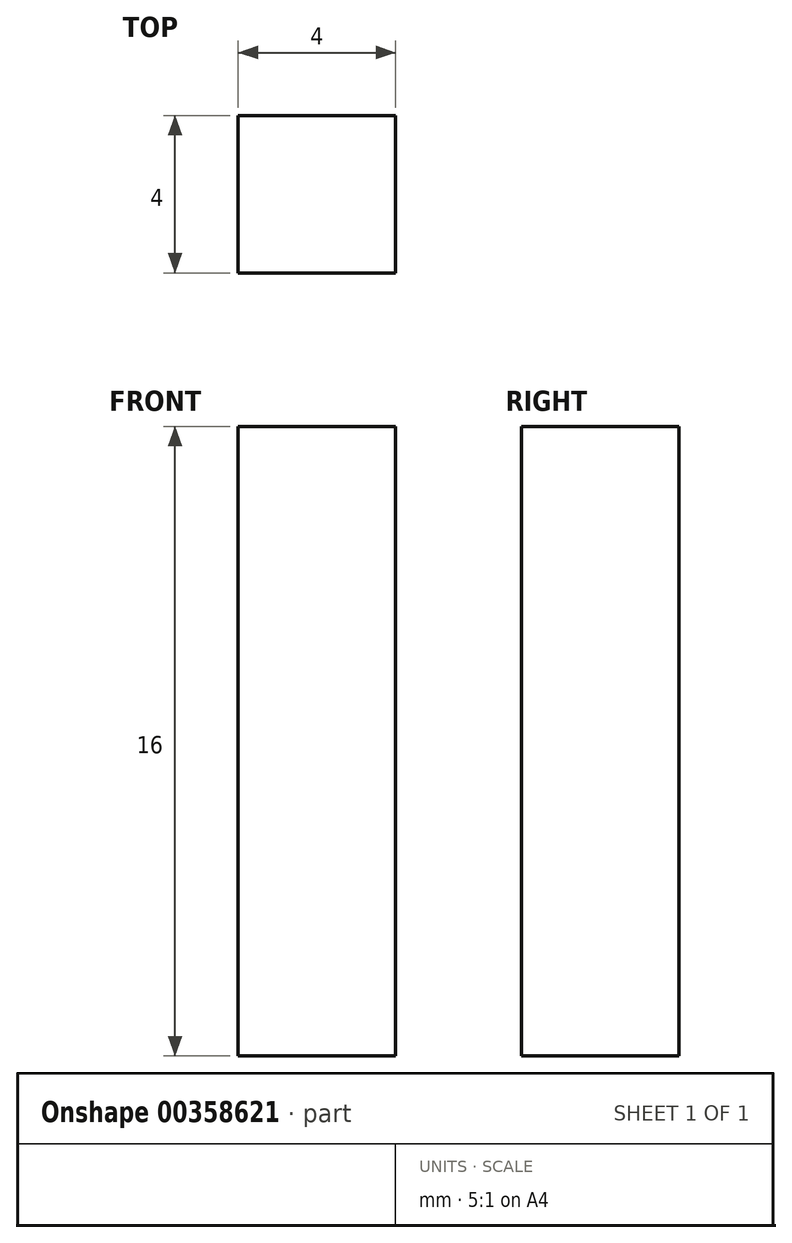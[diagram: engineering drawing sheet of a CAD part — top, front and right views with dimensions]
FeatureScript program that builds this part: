
annotation { "Feature Type Name" : "Feature", "Feature Type Description" : "" }
export const myFeature = defineFeature(function(context is Context, id is Id, definition is map)
    precondition{}
    {
        {
            var Q0;
            Q0=qCreatedBy(makeId("Front.planeOp"),FACE);
            var sketch = newSketch(context, id + "F0", { "sketchPlane" : qUnion([Q0])});
            skLineSegment(sketch, "E0.bottom", {"start": v(-2, 8) * mm, "end": v(2, 8) * mm});
            skLineSegment(sketch, "E0.top", {"start": v(-2, -8) * mm, "end": v(2, -8) * mm});
            skLineSegment(sketch, "E0.left", {"start": v(-2, 8) * mm, "end": v(-2, -8) * mm});
            skLineSegment(sketch, "E0.right", {"start": v(2, 8) * mm, "end": v(2, -8) * mm});
            skPoint(sketch, "E0.middle", {"position": v(0, 0) * mm});
            skSolve(sketch);
        }
        {
            var Q0;
            Q0 = qSketchRegion(id + "F0", true);
            extrude(context, id + "F1", {"entities" : qUnion([Q0]), "depth" : 4 * mm});
        }
    });
